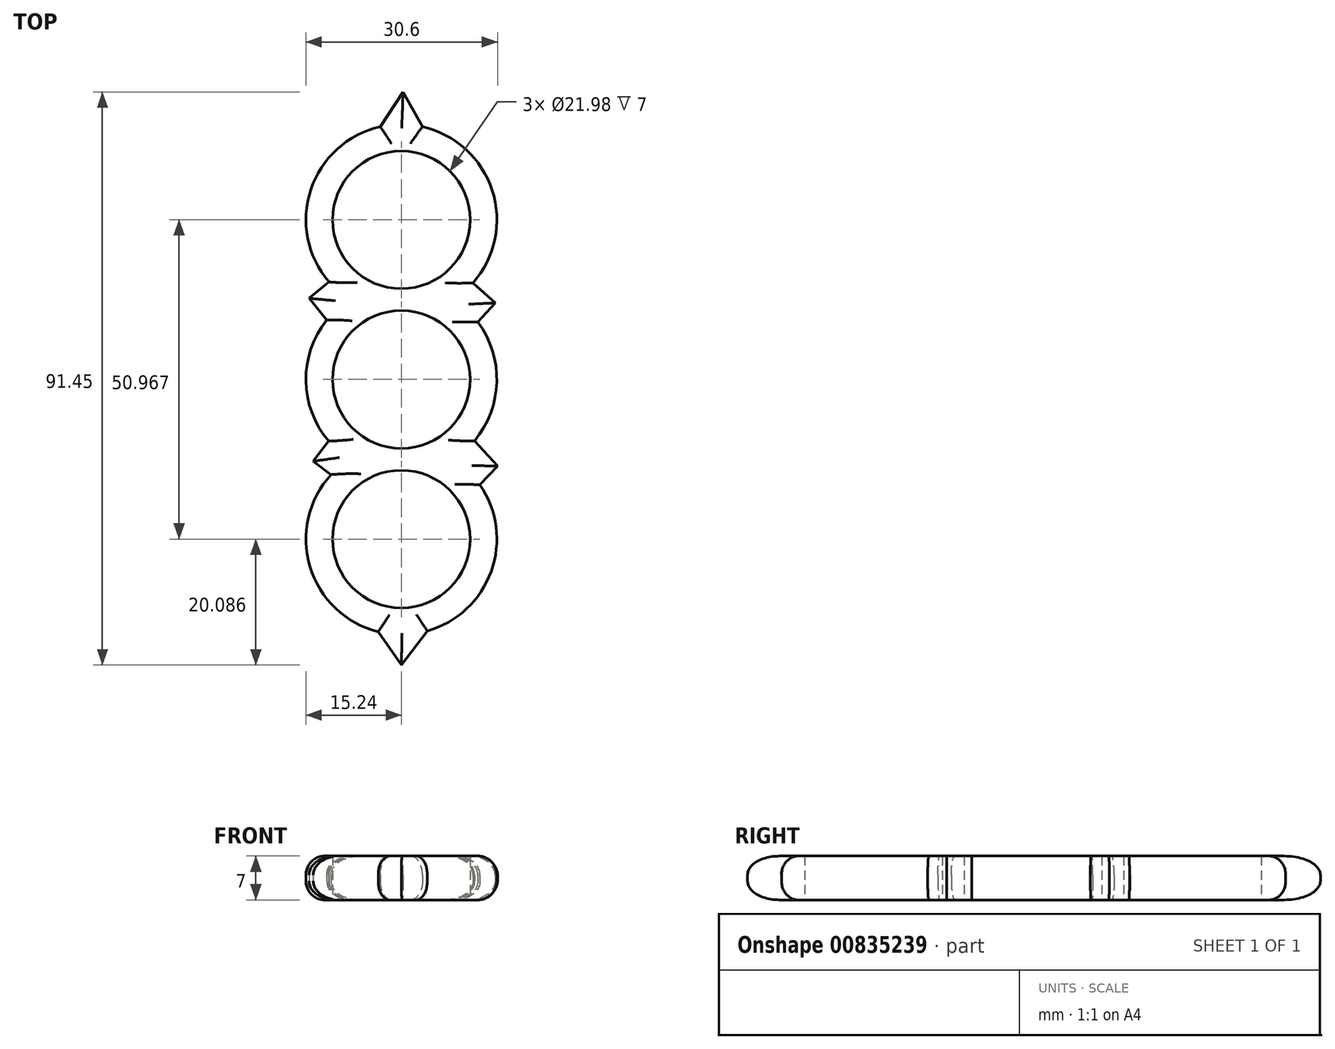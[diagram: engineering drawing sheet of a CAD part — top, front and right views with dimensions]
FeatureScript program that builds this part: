
annotation { "Feature Type Name" : "Feature", "Feature Type Description" : "" }
export const myFeature = defineFeature(function(context is Context, id is Id, definition is map)
    precondition{}
    {
        {
            var Q0;
            Q0=qCreatedBy(makeId("Top.planeOp"),FACE);
            var sketch = newSketch(context, id + "F0", { "sketchPlane" : qUnion([Q0])});
            skCircle(sketch, "E0", {"center": v(0, 0) * mm, "radius": 11 * mm});
            skCircle(sketch, "E1", {"center": v(0, 25.48) * mm, "radius": 11 * mm});
            skCircle(sketch, "E2", {"center": v(0, -25.48) * mm, "radius": 11 * mm});
            skLineSegment(sketch, "E3.bottom", {"start": v(-29.85, 57.15) * mm, "end": v(29.85, 57.15) * mm, "construction": true});
            skLineSegment(sketch, "E3.top", {"start": v(-29.85, -57.15) * mm, "end": v(29.85, -57.15) * mm, "construction": true});
            skLineSegment(sketch, "E3.left", {"start": v(-29.84, 57.15) * mm, "end": v(-29.85, -57.15) * mm, "construction": true});
            skLineSegment(sketch, "E3.right", {"start": v(29.85, 57.15) * mm, "end": v(29.84, -57.15) * mm, "construction": true});
            skPoint(sketch, "E4", {"position": v(0, 57.15) * mm});
            skPoint(sketch, "E5", {"position": v(-29.85, 0) * mm});
            skArc(sketch, "E6", {"start": v(11.45, 15.42) * mm, "mid": v(14.5, 30.19) * mm, "end": v(3.36, 40.35) * mm});
            skArc(sketch, "E7", {"start": v(-11.24, -15.2) * mm, "mid": v(-14.6, -29.87) * mm, "end": v(-3.7, -40.27) * mm});
            skArc(sketch, "E8", {"start": v(-11.9, 9.52) * mm, "mid": v(-15.24, -0.21) * mm, "end": v(-11.64, -9.84) * mm});
            skLineSegment(sketch, "E9", {"start": v(-11.58, 15.57) * mm, "end": v(-14.75, 12.96) * mm});
            skLineSegment(sketch, "E10", {"start": v(-14.75, 12.96) * mm, "end": v(-11.9, 9.52) * mm});
            skLineSegment(sketch, "E11", {"start": v(11.45, 15.42) * mm, "end": v(14.97, 12.22) * mm});
            skLineSegment(sketch, "E12", {"start": v(14.97, 12.22) * mm, "end": v(12.19, 9.15) * mm});
            skLineSegment(sketch, "E13", {"start": v(-11.64, -9.84) * mm, "end": v(-14.07, -13.05) * mm});
            skLineSegment(sketch, "E14", {"start": v(-14.07, -13.05) * mm, "end": v(-11.24, -15.2) * mm});
            skLineSegment(sketch, "E15", {"start": v(-11.24, -15.2) * mm, "end": v(-11.24, -15.2) * mm});
            skLineSegment(sketch, "E16", {"start": v(11.68, -9.8) * mm, "end": v(15.36, -13.79) * mm});
            skLineSegment(sketch, "E17", {"start": v(15.36, -13.79) * mm, "end": v(12.54, -16.82) * mm});
            skLineSegment(sketch, "E18", {"start": v(-3.38, 40.35) * mm, "end": v(0.27, 45.88) * mm});
            skLineSegment(sketch, "E19", {"start": v(0.27, 45.88) * mm, "end": v(3.36, 40.35) * mm});
            skLineSegment(sketch, "E20", {"start": v(-3.7, -40.27) * mm, "end": v(0, -45.57) * mm});
            skLineSegment(sketch, "E21", {"start": v(0, -45.57) * mm, "end": v(4.14, -40.15) * mm});
            skArc(sketch, "E22.trimOffspring", {"start": v(11.68, -9.8) * mm, "mid": v(15.23, -0.41) * mm, "end": v(12.19, 9.15) * mm});
            skArc(sketch, "E23.trimOffspring", {"start": v(4.14, -40.15) * mm, "mid": v(14.34, -30.65) * mm, "end": v(12.54, -16.82) * mm});
            skArc(sketch, "E24.trimOffspring", {"start": v(-3.38, 40.35) * mm, "mid": v(-14.47, 30.27) * mm, "end": v(-11.58, 15.57) * mm});
            skSolve(sketch);
        }
        {
            var Q0;
            Q0 = qSketchRegion(id + "F0", true);
            extrude(context, id + "F1", {"entities" : qUnion([Q0]), "depth" : 7 * mm, "offsetDistance" : 25.4 * mm});
        }
        {
            var Q0;
            Q0=makeQuery(id+"F1.opExtrude","CAP_EDGE",EDGE,{"disambiguationData":[OSD([sQuery(id+"F0.wireOp",EDGE,"E6")])],"isStart":false});
            var Q1;
            Q1=makeQuery(id+"F1.opExtrude","CAP_EDGE",EDGE,{"disambiguationData":[OSD([sQuery(id+"F0.wireOp",EDGE,"E24.trimOffspring")])],"isStart":false});
            var Q2;
            Q2=makeQuery(id+"F1.opExtrude","CAP_EDGE",EDGE,{"disambiguationData":[OSD([sQuery(id+"F0.wireOp",EDGE,"E19")])],"isStart":false});
            var Q3;
            Q3=makeQuery(id+"F1.opExtrude","CAP_EDGE",EDGE,{"disambiguationData":[OSD([sQuery(id+"F0.wireOp",EDGE,"E18")])],"isStart":false});
            var Q4;
            Q4=makeQuery(id+"F1.opExtrude","CAP_EDGE",EDGE,{"disambiguationData":[OSD([sQuery(id+"F0.wireOp",EDGE,"E10")])],"isStart":false});
            var Q5;
            Q5=makeQuery(id+"F1.opExtrude","CAP_EDGE",EDGE,{"disambiguationData":[OSD([sQuery(id+"F0.wireOp",EDGE,"E12")])],"isStart":false});
            var Q6;
            Q6=makeQuery(id+"F1.opExtrude","CAP_EDGE",EDGE,{"disambiguationData":[OSD([sQuery(id+"F0.wireOp",EDGE,"E22.trimOffspring")])],"isStart":false});
            var Q7;
            Q7=makeQuery(id+"F1.opExtrude","CAP_EDGE",EDGE,{"disambiguationData":[OSD([sQuery(id+"F0.wireOp",EDGE,"E11")])],"isStart":false});
            var Q8;
            Q8=makeQuery(id+"F1.opExtrude","CAP_EDGE",EDGE,{"disambiguationData":[OSD([sQuery(id+"F0.wireOp",EDGE,"E9")])],"isStart":false});
            var Q9;
            Q9=makeQuery(id+"F1.opExtrude","CAP_EDGE",EDGE,{"disambiguationData":[OSD([sQuery(id+"F0.wireOp",EDGE,"E8")])],"isStart":false});
            var Q10;
            Q10=makeQuery(id+"F1.opExtrude","CAP_EDGE",EDGE,{"disambiguationData":[OSD([sQuery(id+"F0.wireOp",EDGE,"E13")])],"isStart":false});
            var Q11;
            Q11=makeQuery(id+"F1.opExtrude","CAP_EDGE",EDGE,{"disambiguationData":[OSD([sQuery(id+"F0.wireOp",EDGE,"E14")])],"isStart":false});
            var Q12;
            Q12=makeQuery(id+"F1.opExtrude","CAP_EDGE",EDGE,{"disambiguationData":[OSD([sQuery(id+"F0.wireOp",EDGE,"E16")])],"isStart":false});
            var Q13;
            Q13=makeQuery(id+"F1.opExtrude","CAP_EDGE",EDGE,{"disambiguationData":[OSD([sQuery(id+"F0.wireOp",EDGE,"E23.trimOffspring")])],"isStart":false});
            var Q14;
            Q14=makeQuery(id+"F1.opExtrude","CAP_EDGE",EDGE,{"disambiguationData":[OSD([sQuery(id+"F0.wireOp",EDGE,"E17")])],"isStart":false});
            var Q15;
            Q15=makeQuery(id+"F1.opExtrude","CAP_EDGE",EDGE,{"disambiguationData":[OSD([sQuery(id+"F0.wireOp",EDGE,"E21")])],"isStart":false});
            var Q16;
            Q16=makeQuery(id+"F1.opExtrude","CAP_EDGE",EDGE,{"disambiguationData":[OSD([sQuery(id+"F0.wireOp",EDGE,"E7")])],"isStart":false});
            var Q17;
            Q17=makeQuery(id+"F1.opExtrude","CAP_EDGE",EDGE,{"disambiguationData":[OSD([sQuery(id+"F0.wireOp",EDGE,"E20")])],"isStart":false});
            fillet(context, id + "F2", {"entities" : qUnion([Q0, Q1, Q2, Q3, Q4, Q5, Q6, Q7, Q8, Q9, Q10, Q11, Q12, Q13, Q14, Q15, Q16, Q17]), "radius" : 3 * mm, "tangentPropagation" : true, "allowEdgeOverflow" : false});
        }
        {
            var Q0;
            Q0=makeQuery(id+"F1.opExtrude","CAP_EDGE",EDGE,{"disambiguationData":[OSD([sQuery(id+"F0.wireOp",EDGE,"E18")])],"isStart":true});
            var Q1;
            Q1=makeQuery(id+"F1.opExtrude","CAP_EDGE",EDGE,{"disambiguationData":[OSD([sQuery(id+"F0.wireOp",EDGE,"E24.trimOffspring")])],"isStart":true});
            var Q2;
            Q2=makeQuery(id+"F1.opExtrude","CAP_EDGE",EDGE,{"disambiguationData":[OSD([sQuery(id+"F0.wireOp",EDGE,"E19")])],"isStart":true});
            var Q3;
            Q3=makeQuery(id+"F1.opExtrude","CAP_EDGE",EDGE,{"disambiguationData":[OSD([sQuery(id+"F0.wireOp",EDGE,"E6")])],"isStart":true});
            var Q4;
            Q4=makeQuery(id+"F1.opExtrude","CAP_EDGE",EDGE,{"disambiguationData":[OSD([sQuery(id+"F0.wireOp",EDGE,"E9")])],"isStart":true});
            var Q5;
            Q5=makeQuery(id+"F1.opExtrude","CAP_EDGE",EDGE,{"disambiguationData":[OSD([sQuery(id+"F0.wireOp",EDGE,"E11")])],"isStart":true});
            var Q6;
            Q6=makeQuery(id+"F1.opExtrude","CAP_EDGE",EDGE,{"disambiguationData":[OSD([sQuery(id+"F0.wireOp",EDGE,"E10")])],"isStart":true});
            var Q7;
            Q7=makeQuery(id+"F1.opExtrude","CAP_EDGE",EDGE,{"disambiguationData":[OSD([sQuery(id+"F0.wireOp",EDGE,"E12")])],"isStart":true});
            var Q8;
            Q8=makeQuery(id+"F1.opExtrude","CAP_EDGE",EDGE,{"disambiguationData":[OSD([sQuery(id+"F0.wireOp",EDGE,"E20")])],"isStart":true});
            var Q9;
            Q9=makeQuery(id+"F1.opExtrude","CAP_EDGE",EDGE,{"disambiguationData":[OSD([sQuery(id+"F0.wireOp",EDGE,"E7")])],"isStart":true});
            var Q10;
            Q10=makeQuery(id+"F1.opExtrude","CAP_EDGE",EDGE,{"disambiguationData":[OSD([sQuery(id+"F0.wireOp",EDGE,"E21")])],"isStart":true});
            var Q11;
            Q11=makeQuery(id+"F1.opExtrude","CAP_EDGE",EDGE,{"disambiguationData":[OSD([sQuery(id+"F0.wireOp",EDGE,"E14")])],"isStart":true});
            var Q12;
            Q12=makeQuery(id+"F1.opExtrude","CAP_EDGE",EDGE,{"disambiguationData":[OSD([sQuery(id+"F0.wireOp",EDGE,"E17")])],"isStart":true});
            var Q13;
            Q13=makeQuery(id+"F1.opExtrude","CAP_EDGE",EDGE,{"disambiguationData":[OSD([sQuery(id+"F0.wireOp",EDGE,"E13")])],"isStart":true});
            var Q14;
            Q14=makeQuery(id+"F1.opExtrude","CAP_EDGE",EDGE,{"disambiguationData":[OSD([sQuery(id+"F0.wireOp",EDGE,"E16")])],"isStart":true});
            var Q15;
            Q15=makeQuery(id+"F1.opExtrude","CAP_EDGE",EDGE,{"disambiguationData":[OSD([sQuery(id+"F0.wireOp",EDGE,"E23.trimOffspring")])],"isStart":true});
            var Q16;
            Q16=makeQuery(id+"F1.opExtrude","CAP_EDGE",EDGE,{"disambiguationData":[OSD([sQuery(id+"F0.wireOp",EDGE,"E8")])],"isStart":true});
            var Q17;
            Q17=makeQuery(id+"F1.opExtrude","CAP_EDGE",EDGE,{"disambiguationData":[OSD([sQuery(id+"F0.wireOp",EDGE,"E22.trimOffspring")])],"isStart":true});
            fillet(context, id + "F3", {"entities" : qUnion([Q0, Q1, Q2, Q3, Q4, Q5, Q6, Q7, Q8, Q9, Q10, Q11, Q12, Q13, Q14, Q15, Q16, Q17]), "radius" : 3 * mm, "tangentPropagation" : true, "allowEdgeOverflow" : false});
        }
    });
